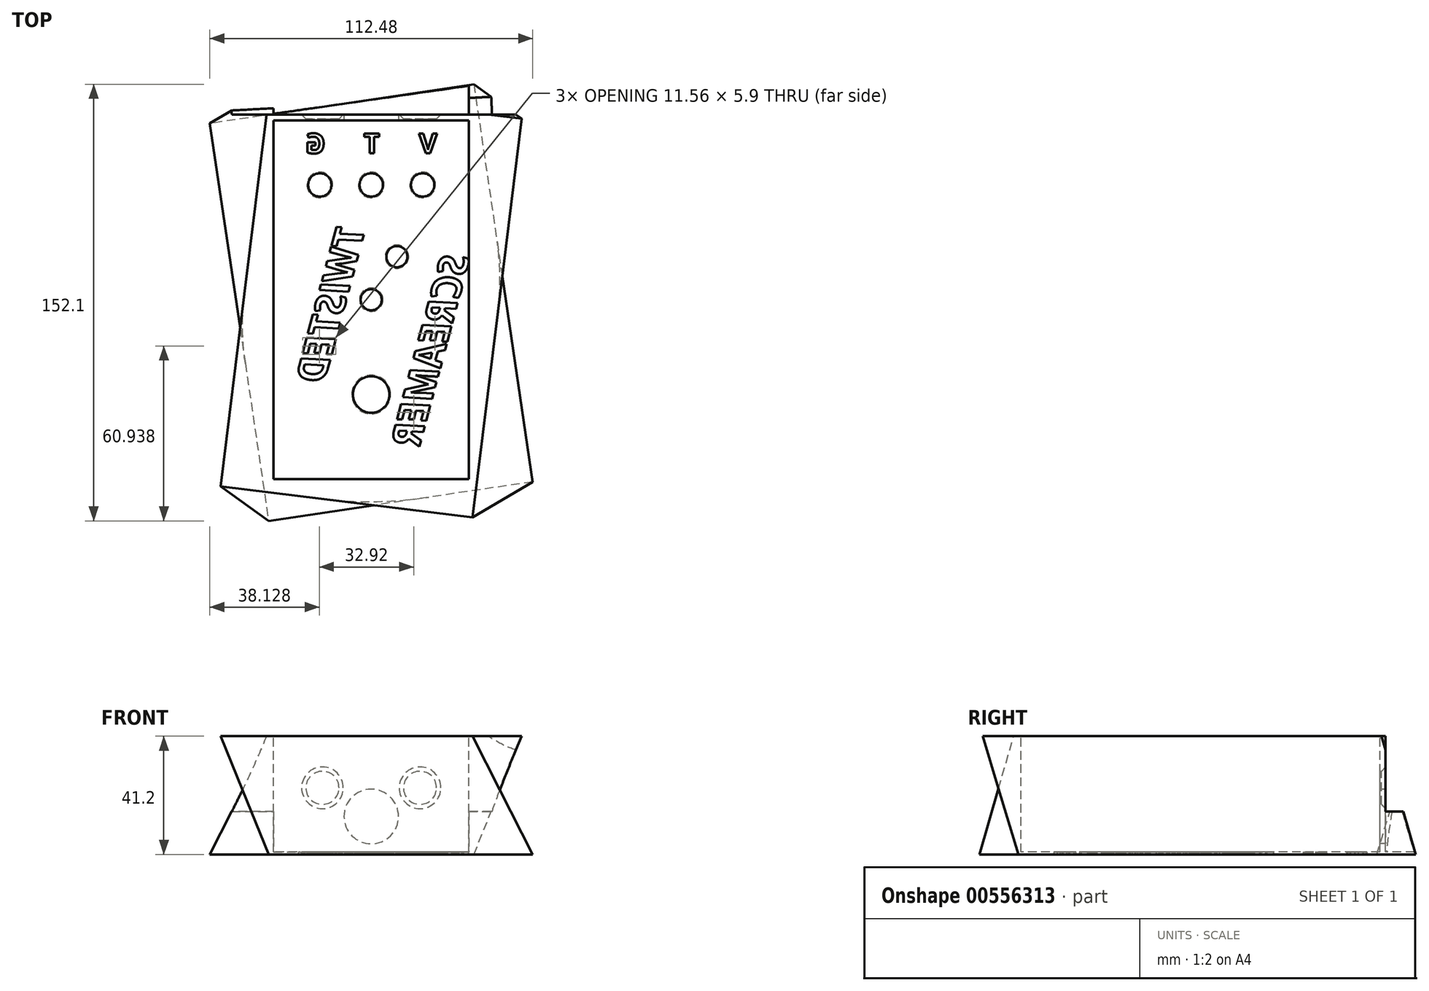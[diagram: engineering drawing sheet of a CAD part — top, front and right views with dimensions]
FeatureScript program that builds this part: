
annotation { "Feature Type Name" : "Feature", "Feature Type Description" : "" }
export const myFeature = defineFeature(function(context is Context, id is Id, definition is map)
    precondition{}
    {
        {
            var Q0;
            Q0=qCreatedBy(makeId("Top.planeOp"),FACE);
            var sketch = newSketch(context, id + "F0", { "sketchPlane" : qUnion([Q0])});
            skLineSegment(sketch, "E0.bottom", {"start": v(-36.5, 64) * mm, "end": v(36.5, 64) * mm});
            skLineSegment(sketch, "E0.top", {"start": v(-36.5, -64) * mm, "end": v(36.5, -64) * mm});
            skLineSegment(sketch, "E0.left", {"start": v(-36.5, 64) * mm, "end": v(-36.5, -64) * mm});
            skLineSegment(sketch, "E0.right", {"start": v(36.5, 64) * mm, "end": v(36.5, -64) * mm});
            skSolve(sketch);
        }
        {
            var Q0;
            Q0=makeQuery(id+"F0.imprint","IMPRINT",FACE,{"disambiguationData":[TD([[makeQuery(id+"F0.imprint","IMPRINT",EDGE,{"derivedFrom":sQuery(id+"F0.wireOp",EDGE,"E0.bottom")}),-1.0]])]});
            extrude(context, id + "F1", {"entities" : qUnion([Q0]), "depth" : 41.2 * mm, "offsetDistance" : 25 * mm});
        }
        {
            var Q0;
            {var subQ0=sQuery(id+"F0.wireOp",EDGE,"E0.bottom");var subQ1=sQuery(id+"F0.wireOp",EDGE,"E0.left");var subQ2=sQuery(id+"F0.wireOp",EDGE,"E0.top");var subQ3=sQuery(id+"F0.wireOp",EDGE,"E0.right");Q0=makeQuery(id+"F16.boolean.opBoolean","SPLIT",FACE,{"disambiguationData":[TD([makeQuery(id+"F1.opExtrude","SWEPT_FACE",FACE,{"disambiguationData":[OSD([subQ0])]})])],"derivedFrom":makeQuery(id+"F1.opExtrude","CAP_FACE",FACE,{"disambiguationData":[OSD([subQ0,subQ2,subQ1,subQ3])],"isStart":true})});}
            var sketch = newSketch(context, id + "F2", { "sketchPlane" : qUnion([Q0])});
            skLineSegment(sketch, "E1.bottom", {"start": v(35.76, -75.05) * mm, "end": v(-56.24, -61.45) * mm});
            skLineSegment(sketch, "E1.top", {"start": v(56.24, 63.45) * mm, "end": v(-35.76, 77.05) * mm});
            skLineSegment(sketch, "E1.left", {"start": v(35.76, -75.05) * mm, "end": v(56.24, 63.45) * mm});
            skLineSegment(sketch, "E1.right", {"start": v(-56.24, -61.45) * mm, "end": v(-35.76, 77.05) * mm});
            skPoint(sketch, "E1.middle", {"position": v(0, 1) * mm});
            skSolve(sketch);
        }
        {
            var Q0;
            Q0=makeQuery(id+"F1.opExtrude","CAP_FACE",FACE,{"disambiguationData":[OSD([sQuery(id+"F0.wireOp",EDGE,"E0.bottom"),sQuery(id+"F0.wireOp",EDGE,"E0.top"),sQuery(id+"F0.wireOp",EDGE,"E0.left"),sQuery(id+"F0.wireOp",EDGE,"E0.right")])],"isStart":false});
            var sketch = newSketch(context, id + "F3", { "sketchPlane" : qUnion([Q0])});
            skLineSegment(sketch, "E2.bottom", {"start": v(-35.35, 73.87) * mm, "end": v(52.41, 63.1) * mm});
            skLineSegment(sketch, "E2.top", {"start": v(-52.41, -65.1) * mm, "end": v(35.35, -75.87) * mm});
            skLineSegment(sketch, "E2.left", {"start": v(-35.35, 73.87) * mm, "end": v(-52.41, -65.1) * mm});
            skLineSegment(sketch, "E2.right", {"start": v(52.41, 63.1) * mm, "end": v(35.35, -75.87) * mm});
            skPoint(sketch, "E2.middle", {"position": v(0, -1) * mm});
            skSolve(sketch);
        }
        {
            var Q1;
            Q1=qSketchRegion(id+"F2",true);
            var Q2;
            Q2=qSketchRegion(id+"F3",true);
            var Q3;
            Q3=sQuery(id+"F2.wireOp",VERTEX,"E1.left.start");
            var Q4;
            Q4=sQuery(id+"F3.wireOp",VERTEX,"E2.right.start");
            loft(context, id + "F4", {"operationType" : NewBodyOperationType.ADD, "sheetProfilesArray" : [{ "sheetProfileEntities" : qUnion([Q1]) }, { "sheetProfileEntities" : qUnion([Q2]) }], "matchConnections" : true, "connections" : [{ "connectionEntities" : qUnion([Q3, Q4]), "connectionEdgeQueries" : qUnion([]), "connectionEdgeParameters" : [] }]});
        }
        {
            var Q0;
            Q0=makeQuery(id+"F1.opExtrude","CAP_FACE",FACE,{"disambiguationData":[OSD([sQuery(id+"F0.wireOp",EDGE,"E0.bottom"),sQuery(id+"F0.wireOp",EDGE,"E0.top"),sQuery(id+"F0.wireOp",EDGE,"E0.left"),sQuery(id+"F0.wireOp",EDGE,"E0.right")])],"isStart":false});
            var sketch = newSketch(context, id + "F5", { "sketchPlane" : qUnion([Q0])});
            skLineSegment(sketch, "E3.bottom", {"start": v(-34, 62.5) * mm, "end": v(34, 62.5) * mm});
            skLineSegment(sketch, "E3.top", {"start": v(-34, -62.5) * mm, "end": v(34, -62.5) * mm});
            skLineSegment(sketch, "E3.left", {"start": v(-34, 62.5) * mm, "end": v(-34, -62.5) * mm});
            skLineSegment(sketch, "E3.right", {"start": v(34, 62.5) * mm, "end": v(34, -62.5) * mm});
            skSolve(sketch);
        }
        {
            var Q0;
            Q0=makeQuery(id+"F5.imprint","IMPRINT",FACE,{"disambiguationData":[TD([[makeQuery(id+"F5.imprint","IMPRINT",EDGE,{"derivedFrom":sQuery(id+"F5.wireOp",EDGE,"E3.bottom")}),-1.0]])]});
            extrude(context, id + "F6", {"entities" : qUnion([Q0]), "operationType" : NewBodyOperationType.REMOVE, "oppositeDirection" : true, "depth" : 40.4 * mm, "offsetDistance" : 25 * mm});
        }
        {
            var Q0;
            Q0=makeQuery(id+"F6.boolean.opBoolean","COPY",FACE,{"derivedFrom":makeQuery(id+"F6.opExtrude","CAP_FACE",FACE,{"disambiguationData":[OSD([sQuery(id+"F5.wireOp",EDGE,"E3.bottom"),sQuery(id+"F5.wireOp",EDGE,"E3.top"),sQuery(id+"F5.wireOp",EDGE,"E3.left"),sQuery(id+"F5.wireOp",EDGE,"E3.right")])],"isStart":false})});
            var sketch = newSketch(context, id + "F7", { "sketchPlane" : qUnion([Q0])});
            skCircle(sketch, "E4", {"center": v(-17.91, 40) * mm, "radius": 4.07 * mm});
            skCircle(sketch, "E5", {"center": v(0, 40) * mm, "radius": 4.07 * mm});
            skCircle(sketch, "E6", {"center": v(17.91, 40) * mm, "radius": 4.07 * mm});
            skCircle(sketch, "E7", {"center": v(0, -33) * mm, "radius": 6.35 * mm});
            skLineSegment(sketch, "E8", {"start": v(17.91, 40) * mm, "end": v(0, 40) * mm, "construction": true});
            skLineSegment(sketch, "E9", {"start": v(8.96, 40) * mm, "end": v(8.96, 15.16) * mm, "construction": true});
            skCircle(sketch, "E10", {"center": v(8.96, 15) * mm, "radius": 3.67 * mm});
            skCircle(sketch, "E11", {"center": v(0, 0) * mm, "radius": 3.67 * mm});
            skSolve(sketch);
        }
        {
            var Q0;
            Q0=qSketchRegion(id+"F7",true);
            extrude(context, id + "F8", {"entities" : qUnion([Q0]), "operationType" : NewBodyOperationType.REMOVE, "oppositeDirection" : true, "depth" : 25 * mm, "offsetDistance" : 25 * mm});
        }
        {
            var Q0;
            Q0=makeQuery(id+"F6.boolean.opBoolean","COPY",FACE,{"derivedFrom":makeQuery(id+"F6.opExtrude","SWEPT_FACE",FACE,{"disambiguationData":[OSD([sQuery(id+"F5.wireOp",EDGE,"E3.bottom")])]})});
            cPlane(context, id + "F9", {"entities" : qUnion([Q0]), "cplaneType" : CPlaneType.OFFSET, "offset" : 2 * mm, "oppositeDirection" : true, "width" : 150 * mm, "height" : 150 * mm});
        }
        {
            var Q0;
            Q0=qCreatedBy(id+"F9.planeOp",FACE);
            var sketch = newSketch(context, id + "F10", { "sketchPlane" : qUnion([Q0])});
            skCircle(sketch, "E12", {"center": v(0, 13.2) * mm, "radius": 9.5 * mm});
            skCircle(sketch, "E13", {"center": v(17, 23.2) * mm, "radius": 5.76 * mm});
            skCircle(sketch, "E14", {"center": v(-17, 23.2) * mm, "radius": 5.76 * mm});
            skSolve(sketch);
        }
        {
            var Q0;
            Q0=qSketchRegion(id+"F10",true);
            extrude(context, id + "F11", {"entities" : qUnion([Q0]), "operationType" : NewBodyOperationType.REMOVE, "endBound" : BoundingType.SYMMETRIC, "oppositeDirection" : true, "depth" : 30 * mm, "offsetDistance" : 25 * mm});
        }
        {
            var Q0;
            Q0=qCreatedBy(id+"F9.planeOp",FACE);
            var sketch = newSketch(context, id + "F12", { "sketchPlane" : qUnion([Q0])});
            skLineSegment(sketch, "E15.0", {"start": v(-34, 0.8) * mm, "end": v(-34, 41.2) * mm});
            skLineSegment(sketch, "E16.0", {"start": v(-34, 0.8) * mm, "end": v(34, 0.8) * mm});
            skLineSegment(sketch, "E17.0", {"start": v(34, 0.8) * mm, "end": v(34, 41.2) * mm});
            skLineSegment(sketch, "E18.0", {"start": v(-34, 41.2) * mm, "end": v(34, 41.2) * mm});
            skSolve(sketch);
        }
        {
            var Q0;
            Q0=qSketchRegion(id+"F12",true);
            extrude(context, id + "F13", {"entities" : qUnion([Q0]), "operationType" : NewBodyOperationType.REMOVE, "oppositeDirection" : true, "depth" : 25 * mm, "offsetDistance" : 25 * mm});
        }
        {
            var Q0;
            Q0=qCreatedBy(makeId("Front.planeOp"),FACE);
            cPlane(context, id + "F14", {"entities" : qUnion([Q0]), "cplaneType" : CPlaneType.OFFSET, "offset" : 38 * mm, "width" : 150 * mm, "height" : 150 * mm});
        }
        {
            var Q0;
            Q0=makeQuery(id+"F1.opExtrude","CAP_FACE",FACE,{"disambiguationData":[OSD([sQuery(id+"F0.wireOp",EDGE,"E0.bottom"),sQuery(id+"F0.wireOp",EDGE,"E0.top"),sQuery(id+"F0.wireOp",EDGE,"E0.left"),sQuery(id+"F0.wireOp",EDGE,"E0.right")])],"isStart":true});
            var sketch = newSketch(context, id + "F15", { "sketchPlane" : qUnion([Q0])});
            skText(sketch, "E19", { "text": "V", "fontName": "OpenSans-Bold.ttf"});
            skText(sketch, "E20", { "text": "T", "fontName": "OpenSans-Bold.ttf"});
            skText(sketch, "E21", { "text": "G", "fontName": "OpenSans-Bold.ttf"});
            const initialGuessF15  = {"E19": [0.02295, -0.051, -1, 0, 0.007], "E20": [0.00303, -0.051, -1, 0, 0.007], "E21": [-0.016, -0.051, -1, 0, 0.007]};
            skSetInitialGuess(sketch, initialGuessF15);
            skSolve(sketch);
        }
        {
            var Q0;
            Q0=qSketchRegion(id+"F15",true);
            extrude(context, id + "F16", {"entities" : qUnion([Q0]), "operationType" : NewBodyOperationType.REMOVE, "endBound" : BoundingType.THROUGH_ALL, "oppositeDirection" : true, "depth" : 0.5 * mm, "offsetDistance" : 25 * mm});
        }
        {
            var Q0;
            Q0=makeQuery(id+"F13.boolean.opBoolean","COPY",FACE,{"derivedFrom":makeQuery(id+"F13.opExtrude","CAP_FACE",FACE,{"disambiguationData":[OSD([sQuery(id+"F12.wireOp",EDGE,"E15.0"),sQuery(id+"F12.wireOp",EDGE,"E16.0"),sQuery(id+"F12.wireOp",EDGE,"E17.0"),sQuery(id+"F12.wireOp",EDGE,"E18.0")])],"isStart":true})});
            var sketch = newSketch(context, id + "F17", { "sketchPlane" : qUnion([Q0])});
            skLineSegment(sketch, "E22", {"start": v(75, 14.96) * mm, "end": v(-75, 14.96) * mm});
            skLineSegment(sketch, "E23", {"start": v(-75, 14.96) * mm, "end": v(-75, 44.5) * mm});
            skLineSegment(sketch, "E24", {"start": v(-75, 44.5) * mm, "end": v(75, 44.5) * mm});
            skLineSegment(sketch, "E25", {"start": v(75, 44.5) * mm, "end": v(75, 14.96) * mm});
            skSolve(sketch);
        }
        {
            var Q0;
            Q0 = qSketchRegion(id + "F17", true);
            extrude(context, id + "F18", {"entities" : qUnion([Q0]), "operationType" : NewBodyOperationType.REMOVE, "depth" : 15 * mm, "offsetDistance" : 25 * mm});
        }
        {
            var Q0;
            Q0=makeQuery(id+"F13.boolean.opBoolean","INTERSECT",EDGE,{"derivedFrom":[makeQuery(id+"F11.boolean.opBoolean","COPY",FACE,{"derivedFrom":makeQuery(id+"F11.opExtrude","SWEPT_FACE",FACE,{"disambiguationData":[OSD([sQuery(id+"F10.wireOp",EDGE,"E14")])]})}),makeQuery(id+"F13.opExtrude","CAP_FACE",FACE,{"disambiguationData":[OSD([sQuery(id+"F12.wireOp",EDGE,"E15.0"),sQuery(id+"F12.wireOp",EDGE,"E16.0"),sQuery(id+"F12.wireOp",EDGE,"E17.0"),sQuery(id+"F12.wireOp",EDGE,"E18.0")])],"isStart":true})]});
            var Q1;
            Q1=makeQuery(id+"F13.boolean.opBoolean","INTERSECT",EDGE,{"derivedFrom":[makeQuery(id+"F11.boolean.opBoolean","COPY",FACE,{"derivedFrom":makeQuery(id+"F11.opExtrude","SWEPT_FACE",FACE,{"disambiguationData":[OSD([sQuery(id+"F10.wireOp",EDGE,"E13")])]})}),makeQuery(id+"F13.opExtrude","CAP_FACE",FACE,{"disambiguationData":[OSD([sQuery(id+"F12.wireOp",EDGE,"E15.0"),sQuery(id+"F12.wireOp",EDGE,"E16.0"),sQuery(id+"F12.wireOp",EDGE,"E17.0"),sQuery(id+"F12.wireOp",EDGE,"E18.0")])],"isStart":true})]});
            chamfer(context, id + "F19", {"entities" : qUnion([Q0, Q1]), "width" : 1.5 * mm, "tangentPropagation" : true});
        }
        {
            var Q0;
            {var subQ0=sQuery(id+"F0.wireOp",EDGE,"E0.bottom");var subQ1=sQuery(id+"F0.wireOp",EDGE,"E0.top");var subQ2=sQuery(id+"F0.wireOp",EDGE,"E0.left");var subQ3=sQuery(id+"F0.wireOp",EDGE,"E0.right");Q0=makeQuery(id+"F8.boolean.opBoolean","INTERSECT",EDGE,{"derivedFrom":[makeQuery(id+"F4.boolean.opBoolean","MERGE",FACE,{"derivedFrom":[makeQuery(id+"F1.opExtrude","CAP_FACE",FACE,{"disambiguationData":[OSD([subQ0,subQ1,subQ2,subQ3])],"isStart":true}),makeQuery(id+"F4.opLoft","CAP_FACE",FACE,{"disambiguationData":[OSD([makeQuery(id+"F2.imprint","IMPRINT",FACE,{"disambiguationData":[TD([[makeQuery(id+"F2.imprint","IMPRINT",EDGE,{"derivedFrom":makeQuery(id+"F1.opExtrude","CAP_EDGE",EDGE,{"disambiguationData":[OSD([subQ0])],"isStart":true})}),1.0]])]})])],"isStart":true})]}),makeQuery(id+"F8.opExtrude","SWEPT_FACE",FACE,{"disambiguationData":[OSD([sQuery(id+"F7.wireOp",EDGE,"E6")])]})]});}
            var Q1;
            {var subQ0=sQuery(id+"F0.wireOp",EDGE,"E0.bottom");var subQ1=sQuery(id+"F0.wireOp",EDGE,"E0.top");var subQ2=sQuery(id+"F0.wireOp",EDGE,"E0.left");var subQ3=sQuery(id+"F0.wireOp",EDGE,"E0.right");Q1=makeQuery(id+"F8.boolean.opBoolean","INTERSECT",EDGE,{"derivedFrom":[makeQuery(id+"F4.boolean.opBoolean","MERGE",FACE,{"derivedFrom":[makeQuery(id+"F1.opExtrude","CAP_FACE",FACE,{"disambiguationData":[OSD([subQ0,subQ1,subQ2,subQ3])],"isStart":true}),makeQuery(id+"F4.opLoft","CAP_FACE",FACE,{"disambiguationData":[OSD([makeQuery(id+"F2.imprint","IMPRINT",FACE,{"disambiguationData":[TD([[makeQuery(id+"F2.imprint","IMPRINT",EDGE,{"derivedFrom":makeQuery(id+"F1.opExtrude","CAP_EDGE",EDGE,{"disambiguationData":[OSD([subQ0])],"isStart":true})}),1.0]])]})])],"isStart":true})]}),makeQuery(id+"F8.opExtrude","SWEPT_FACE",FACE,{"disambiguationData":[OSD([sQuery(id+"F7.wireOp",EDGE,"E5")])]})]});}
            var Q2;
            {var subQ0=sQuery(id+"F0.wireOp",EDGE,"E0.bottom");var subQ1=sQuery(id+"F0.wireOp",EDGE,"E0.top");var subQ2=sQuery(id+"F0.wireOp",EDGE,"E0.left");var subQ3=sQuery(id+"F0.wireOp",EDGE,"E0.right");Q2=makeQuery(id+"F8.boolean.opBoolean","INTERSECT",EDGE,{"derivedFrom":[makeQuery(id+"F4.boolean.opBoolean","MERGE",FACE,{"derivedFrom":[makeQuery(id+"F1.opExtrude","CAP_FACE",FACE,{"disambiguationData":[OSD([subQ0,subQ1,subQ2,subQ3])],"isStart":true}),makeQuery(id+"F4.opLoft","CAP_FACE",FACE,{"disambiguationData":[OSD([makeQuery(id+"F2.imprint","IMPRINT",FACE,{"disambiguationData":[TD([[makeQuery(id+"F2.imprint","IMPRINT",EDGE,{"derivedFrom":makeQuery(id+"F1.opExtrude","CAP_EDGE",EDGE,{"disambiguationData":[OSD([subQ0])],"isStart":true})}),1.0]])]})])],"isStart":true})]}),makeQuery(id+"F8.opExtrude","SWEPT_FACE",FACE,{"disambiguationData":[OSD([sQuery(id+"F7.wireOp",EDGE,"E4")])]})]});}
            var Q3;
            {var subQ0=sQuery(id+"F0.wireOp",EDGE,"E0.bottom");var subQ1=sQuery(id+"F0.wireOp",EDGE,"E0.top");var subQ2=sQuery(id+"F0.wireOp",EDGE,"E0.left");var subQ3=sQuery(id+"F0.wireOp",EDGE,"E0.right");Q3=makeQuery(id+"F8.boolean.opBoolean","INTERSECT",EDGE,{"derivedFrom":[makeQuery(id+"F4.boolean.opBoolean","MERGE",FACE,{"derivedFrom":[makeQuery(id+"F1.opExtrude","CAP_FACE",FACE,{"disambiguationData":[OSD([subQ0,subQ1,subQ2,subQ3])],"isStart":true}),makeQuery(id+"F4.opLoft","CAP_FACE",FACE,{"disambiguationData":[OSD([makeQuery(id+"F2.imprint","IMPRINT",FACE,{"disambiguationData":[TD([[makeQuery(id+"F2.imprint","IMPRINT",EDGE,{"derivedFrom":makeQuery(id+"F1.opExtrude","CAP_EDGE",EDGE,{"disambiguationData":[OSD([subQ0])],"isStart":true})}),1.0]])]})])],"isStart":true})]}),makeQuery(id+"F8.opExtrude","SWEPT_FACE",FACE,{"disambiguationData":[OSD([sQuery(id+"F7.wireOp",EDGE,"E10")])]})]});}
            var Q4;
            {var subQ0=sQuery(id+"F0.wireOp",EDGE,"E0.bottom");var subQ1=sQuery(id+"F0.wireOp",EDGE,"E0.top");var subQ2=sQuery(id+"F0.wireOp",EDGE,"E0.left");var subQ3=sQuery(id+"F0.wireOp",EDGE,"E0.right");Q4=makeQuery(id+"F8.boolean.opBoolean","INTERSECT",EDGE,{"derivedFrom":[makeQuery(id+"F4.boolean.opBoolean","MERGE",FACE,{"derivedFrom":[makeQuery(id+"F1.opExtrude","CAP_FACE",FACE,{"disambiguationData":[OSD([subQ0,subQ1,subQ2,subQ3])],"isStart":true}),makeQuery(id+"F4.opLoft","CAP_FACE",FACE,{"disambiguationData":[OSD([makeQuery(id+"F2.imprint","IMPRINT",FACE,{"disambiguationData":[TD([[makeQuery(id+"F2.imprint","IMPRINT",EDGE,{"derivedFrom":makeQuery(id+"F1.opExtrude","CAP_EDGE",EDGE,{"disambiguationData":[OSD([subQ0])],"isStart":true})}),1.0]])]})])],"isStart":true})]}),makeQuery(id+"F8.opExtrude","SWEPT_FACE",FACE,{"disambiguationData":[OSD([sQuery(id+"F7.wireOp",EDGE,"E11")])]})]});}
            var Q5;
            {var subQ0=sQuery(id+"F0.wireOp",EDGE,"E0.bottom");var subQ1=sQuery(id+"F0.wireOp",EDGE,"E0.top");var subQ2=sQuery(id+"F0.wireOp",EDGE,"E0.left");var subQ3=sQuery(id+"F0.wireOp",EDGE,"E0.right");Q5=makeQuery(id+"F8.boolean.opBoolean","INTERSECT",EDGE,{"derivedFrom":[makeQuery(id+"F4.boolean.opBoolean","MERGE",FACE,{"derivedFrom":[makeQuery(id+"F1.opExtrude","CAP_FACE",FACE,{"disambiguationData":[OSD([subQ0,subQ1,subQ2,subQ3])],"isStart":true}),makeQuery(id+"F4.opLoft","CAP_FACE",FACE,{"disambiguationData":[OSD([makeQuery(id+"F2.imprint","IMPRINT",FACE,{"disambiguationData":[TD([[makeQuery(id+"F2.imprint","IMPRINT",EDGE,{"derivedFrom":makeQuery(id+"F1.opExtrude","CAP_EDGE",EDGE,{"disambiguationData":[OSD([subQ0])],"isStart":true})}),1.0]])]})])],"isStart":true})]}),makeQuery(id+"F8.opExtrude","SWEPT_FACE",FACE,{"disambiguationData":[OSD([sQuery(id+"F7.wireOp",EDGE,"E7")])]})]});}
            chamfer(context, id + "F20", {"entities" : qUnion([Q0, Q1, Q2, Q3, Q4, Q5]), "width" : 0.4 * mm, "tangentPropagation" : true});
        }
        {
            var Q0;
            {var subQ0=sQuery(id+"F0.wireOp",EDGE,"E0.bottom");var subQ1=sQuery(id+"F0.wireOp",EDGE,"E0.top");var subQ2=sQuery(id+"F0.wireOp",EDGE,"E0.left");var subQ3=sQuery(id+"F0.wireOp",EDGE,"E0.right");Q0=makeQuery(id+"F4.boolean.opBoolean","MERGE",FACE,{"derivedFrom":[makeQuery(id+"F1.opExtrude","CAP_FACE",FACE,{"disambiguationData":[OSD([subQ0,subQ1,subQ2,subQ3])],"isStart":true}),makeQuery(id+"F4.opLoft","CAP_FACE",FACE,{"disambiguationData":[OSD([makeQuery(id+"F2.imprint","IMPRINT",FACE,{"disambiguationData":[TD([[makeQuery(id+"F2.imprint","IMPRINT",EDGE,{"derivedFrom":makeQuery(id+"F1.opExtrude","CAP_EDGE",EDGE,{"disambiguationData":[OSD([subQ0])],"isStart":true})}),1.0]])]})])],"isStart":true})]});}
            var sketch = newSketch(context, id + "F21", { "sketchPlane" : qUnion([Q0])});
            skText(sketch, "E26", { "text": "TWISTED\n\nSCREAMER", "fontName": "OpenSans-BoldItalic.ttf"});
            const initialGuessF21  = {"E26": [-0.00215, -0.0243, -0.25882, 0.96593, 0.01]};
            skSetInitialGuess(sketch, initialGuessF21);
            skSolve(sketch);
        }
        {
            var Q0;
            Q0 = qSketchRegion(id + "F21", true);
            extrude(context, id + "F22", {"entities" : qUnion([Q0]), "operationType" : NewBodyOperationType.REMOVE, "endBound" : BoundingType.THROUGH_ALL, "oppositeDirection" : true, "depth" : 25 * mm, "offsetDistance" : 25 * mm});
        }
    });
